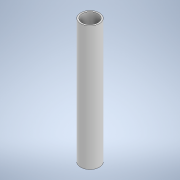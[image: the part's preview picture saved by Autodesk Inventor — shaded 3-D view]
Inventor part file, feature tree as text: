
AUTODESK INVENTOR PART (.ipt)
format: ipt  version: 2022 (Build 260153000, 153)  size: 99,840 bytes
history: native  units: mm
features: other x1, extrude x1, sketch x1
ambient origin geometry x8: Origin, YZ Plane, XZ Plane, XY Plane, X Axis, Y Axis, Z Axis, Center Point
bodies: Body1 (feature_tree)
feature tree (3):
  other  "Sólido1"
  extrude  "Extrusión1"  Depth=141.29mm
  sketch  "Boceto1"  dims[d0=21.36mm d1=17.92mm d2=141.29mm d3=0.0mm]
